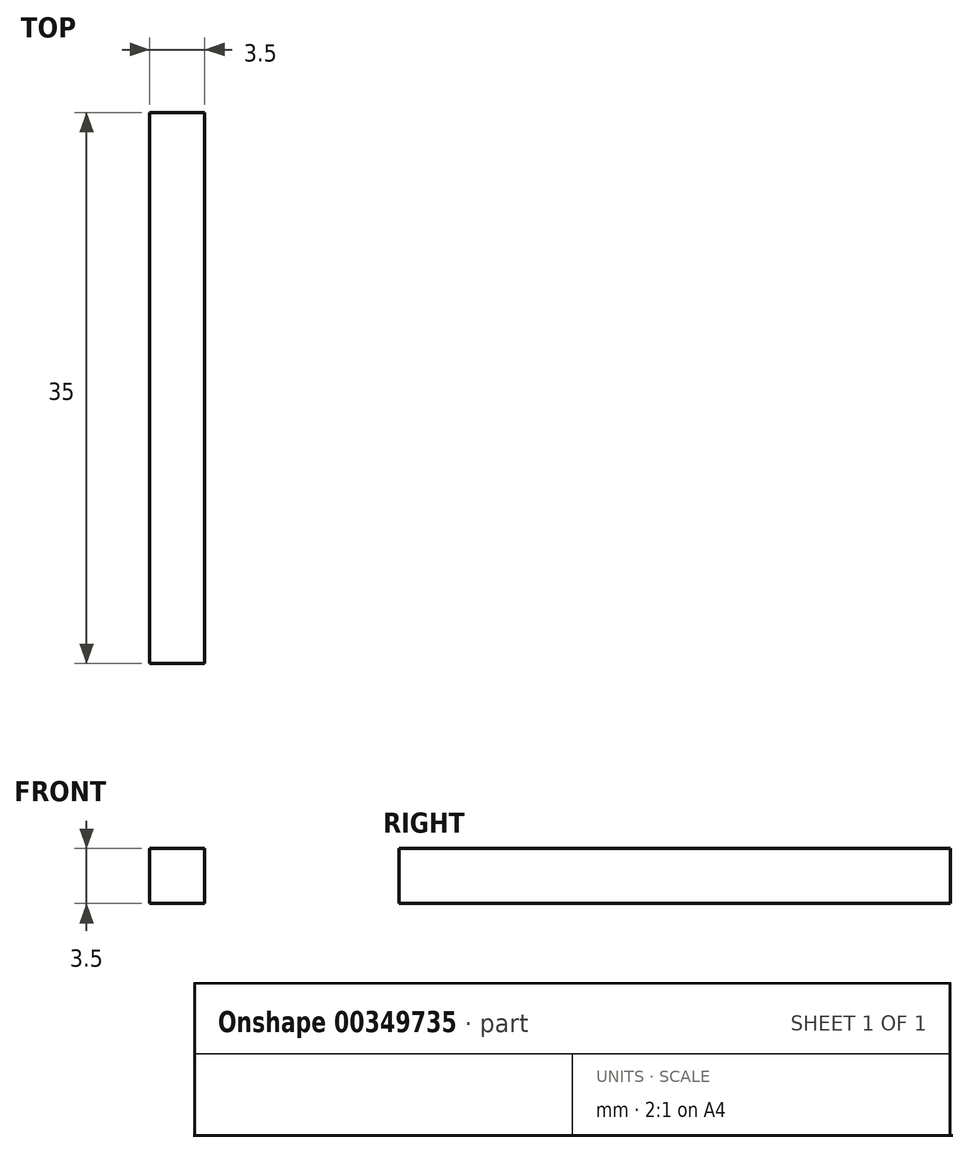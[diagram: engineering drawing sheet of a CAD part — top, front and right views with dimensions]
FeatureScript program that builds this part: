
annotation { "Feature Type Name" : "Feature", "Feature Type Description" : "" }
export const myFeature = defineFeature(function(context is Context, id is Id, definition is map)
    precondition{}
    {
        {
            var Q0;
            Q0=qCreatedBy(makeId("Top.planeOp"),FACE);
            var sketch = newSketch(context, id + "F0", { "sketchPlane" : qUnion([Q0])});
            skLineSegment(sketch, "E0.bottom", {"start": v(1.75, -17.5) * mm, "end": v(-1.75, -17.5) * mm});
            skLineSegment(sketch, "E0.top", {"start": v(1.75, 17.5) * mm, "end": v(-1.75, 17.5) * mm});
            skLineSegment(sketch, "E0.left", {"start": v(1.75, -17.5) * mm, "end": v(1.75, 17.5) * mm});
            skLineSegment(sketch, "E0.right", {"start": v(-1.75, -17.5) * mm, "end": v(-1.75, 17.5) * mm});
            skPoint(sketch, "E0.middle", {"position": v(0, 0) * mm});
            skSolve(sketch);
        }
        {
            var Q0;
            Q0=qSketchRegion(id+"F0",true);
            extrude(context, id + "F1", {"entities" : qUnion([Q0]), "depth" : 3.5 * mm});
        }
    });
